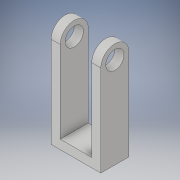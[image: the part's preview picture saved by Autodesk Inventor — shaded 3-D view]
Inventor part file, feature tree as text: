
AUTODESK INVENTOR PART (.ipt)
format: ipt  version: 2017 (Build 210142000, 142)  size: 119,296 bytes
history: native  units: in
note: dims shown in document units (in); Inventor stores cm internally (conversion verified against a paired STEP export)
features: extrude x2, sketch x2
ambient origin geometry x8: Origin, YZ Plane, XZ Plane, XY Plane, X Axis, Y Axis, Z Axis, Center Point
bodies: Solid1 (feature_tree)
feature tree (4):
  extrude  "Extrusion1"  Depth=0.77in
  extrude  "Extrusion2"  Depth=0.77in
  sketch  "Sketch1"  dims[d0=0.5in d1=0.77in]
  sketch  "Sketch2"  dims[d2=2.5in d3=0.77in d4=1.365in d5=0.0in d8=0.25in d10=1.26in d11=0.0in d12=0.25in d13=0.25in]
